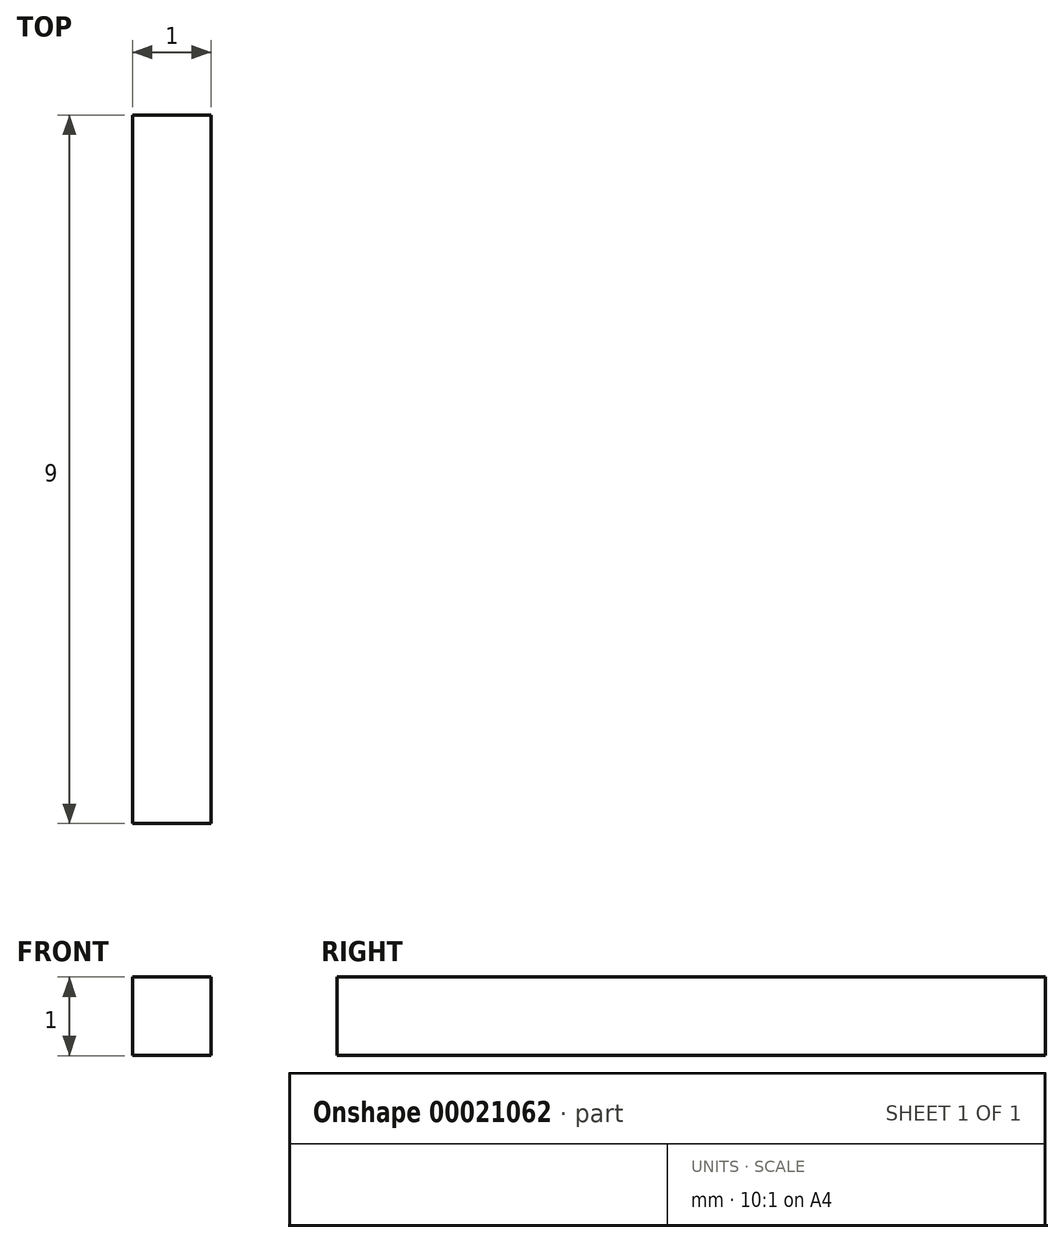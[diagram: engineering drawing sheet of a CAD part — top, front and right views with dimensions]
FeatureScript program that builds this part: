
annotation { "Feature Type Name" : "Feature", "Feature Type Description" : "" }
export const myFeature = defineFeature(function(context is Context, id is Id, definition is map)
    precondition{}
    {
        {
            var Q0;
            Q0=qCreatedBy(makeId("Front.planeOp"),FACE);
            var sketch = newSketch(context, id + "F0", { "sketchPlane" : qUnion([Q0])});
            skLineSegment(sketch, "E0.bottom", {"start": v(-27.28, 23.26) * mm, "end": v(-26.28, 23.26) * mm});
            skLineSegment(sketch, "E0.top", {"start": v(-27.28, 22.26) * mm, "end": v(-26.28, 22.26) * mm});
            skLineSegment(sketch, "E0.left", {"start": v(-27.28, 23.26) * mm, "end": v(-27.28, 22.26) * mm});
            skLineSegment(sketch, "E0.right", {"start": v(-26.28, 23.26) * mm, "end": v(-26.28, 22.26) * mm});
            skSolve(sketch);
        }
        {
            var Q0;
            Q0 = qSketchRegion(id + "F0", true);
            extrude(context, id + "F1", {"entities" : qUnion([Q0]), "depth" : 9 * mm});
        }
    });
